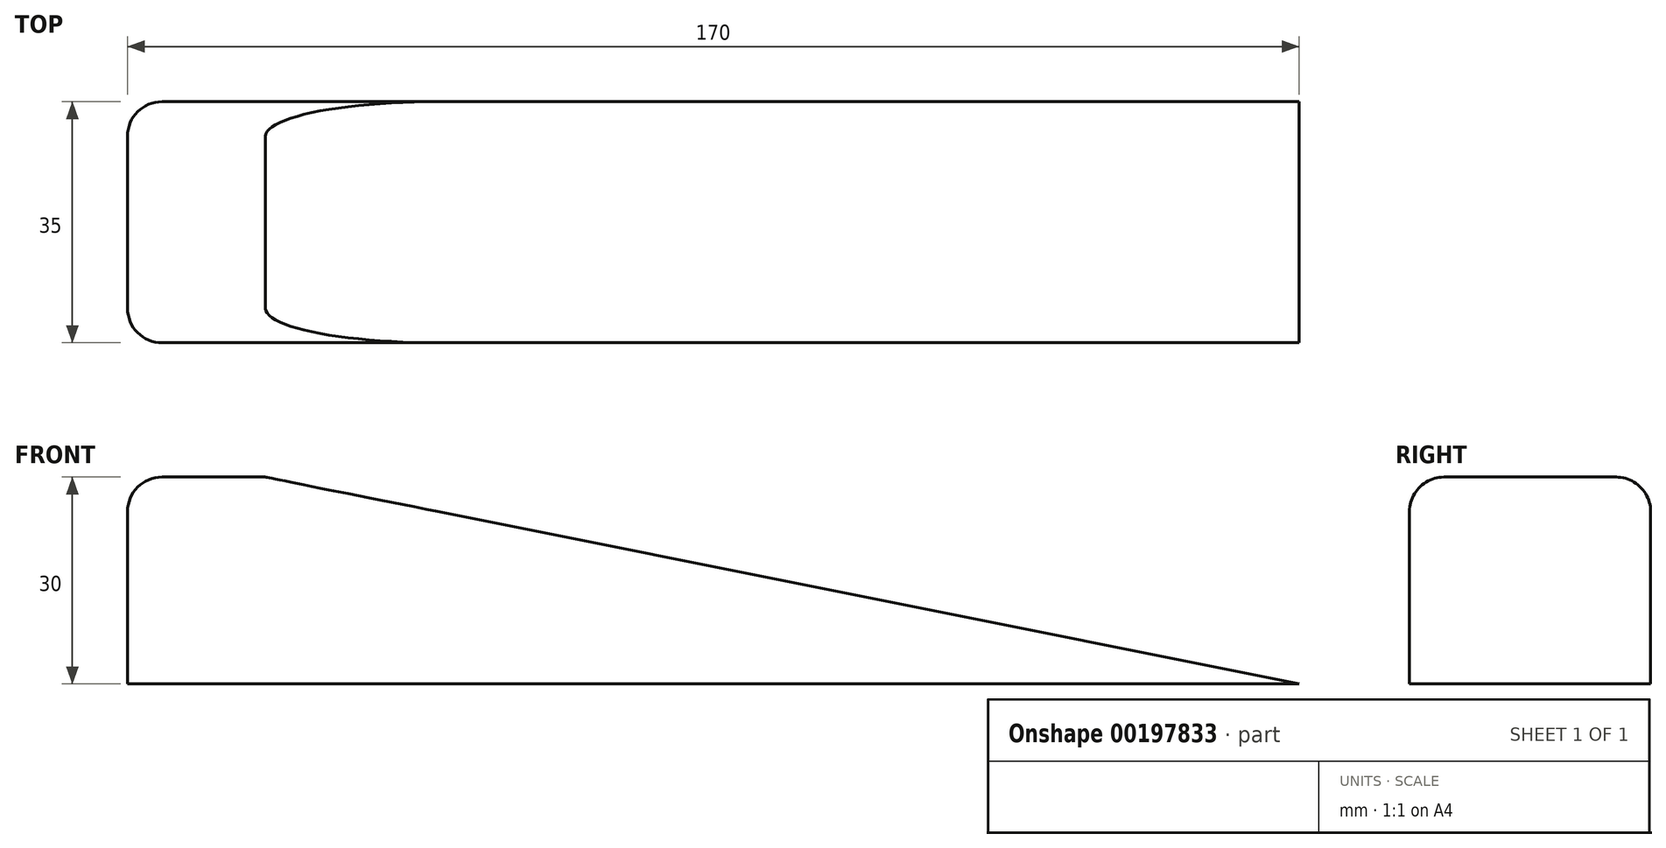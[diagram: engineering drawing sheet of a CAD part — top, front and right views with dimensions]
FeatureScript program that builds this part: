
annotation { "Feature Type Name" : "Feature", "Feature Type Description" : "" }
export const myFeature = defineFeature(function(context is Context, id is Id, definition is map)
    precondition{}
    {
        {
            var Q0;
            Q0=qCreatedBy(makeId("Front.planeOp"),FACE);
            var sketch = newSketch(context, id + "F0", { "sketchPlane" : qUnion([Q0])});
            skLineSegment(sketch, "E0.bottom", {"start": v(-10, 15) * mm, "end": v(10, 15) * mm});
            skLineSegment(sketch, "E0.top", {"start": v(-10, -15) * mm, "end": v(10, -15) * mm});
            skLineSegment(sketch, "E0.left", {"start": v(-10, 15) * mm, "end": v(-10, -15) * mm});
            skLineSegment(sketch, "E0.right", {"start": v(10, 15) * mm, "end": v(10, -15) * mm});
            skPoint(sketch, "E0.middle", {"position": v(0, 0) * mm});
            skLineSegment(sketch, "E1", {"start": v(10, -15) * mm, "end": v(160, -15) * mm});
            skLineSegment(sketch, "E2", {"start": v(10, 15) * mm, "end": v(160, -15) * mm});
            skSolve(sketch);
        }
        {
            var Q0;
            Q0 = qSketchRegion(id + "F0", true);
            extrude(context, id + "F1", {"entities" : qUnion([Q0]), "endBound" : BoundingType.SYMMETRIC, "depth" : 35 * mm});
        }
        {
            var Q0;
            Q0=makeQuery(id+"F1.opExtrude","SWEPT_EDGE",EDGE,{"disambiguationData":[OSD([sQuery(id+"F0.wireOp",EDGE,"E0.bottom"),sQuery(id+"F0.wireOp",EDGE,"E0.left")])]});
            var Q1;
            Q1=makeQuery(id+"F1.opExtrude","CAP_EDGE",EDGE,{"disambiguationData":[OSD([sQuery(id+"F0.wireOp",EDGE,"E0.left")])],"isStart":false});
            var Q2;
            Q2=makeQuery(id+"F1.opExtrude","CAP_EDGE",EDGE,{"disambiguationData":[OSD([sQuery(id+"F0.wireOp",EDGE,"E0.left")])],"isStart":true});
            var Q3;
            Q3=makeQuery(id+"F1.opExtrude","CAP_EDGE",EDGE,{"disambiguationData":[OSD([sQuery(id+"F0.wireOp",EDGE,"E0.bottom")])],"isStart":false});
            var Q4;
            Q4=makeQuery(id+"F1.opExtrude","CAP_EDGE",EDGE,{"disambiguationData":[OSD([sQuery(id+"F0.wireOp",EDGE,"E0.bottom")])],"isStart":true});
            fillet(context, id + "F2", {"entities" : qUnion([Q0, Q1, Q2, Q3, Q4]), "radius" : 5 * mm, "tangentPropagation" : true, "allowEdgeOverflow" : false});
        }
    });
